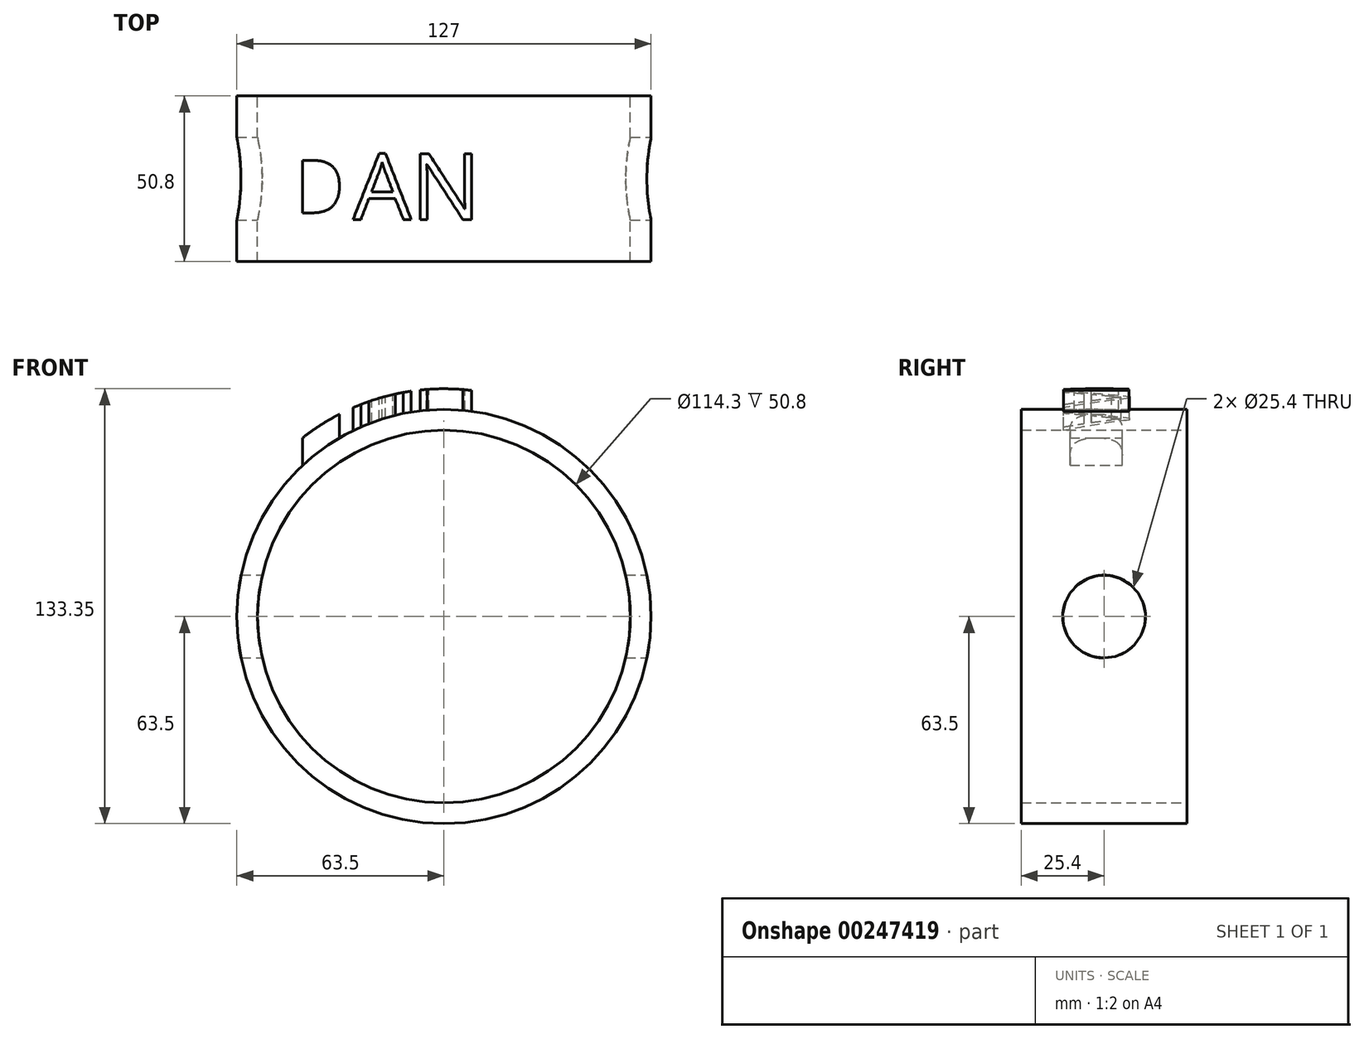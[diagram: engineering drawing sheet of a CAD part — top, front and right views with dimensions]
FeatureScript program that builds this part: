
annotation { "Feature Type Name" : "Feature", "Feature Type Description" : "" }
export const myFeature = defineFeature(function(context is Context, id is Id, definition is map)
    precondition{}
    {
        {
            var Q0;
            Q0=qCreatedBy(makeId("Front.planeOp"),FACE);
            var sketch = newSketch(context, id + "F0", { "sketchPlane" : qUnion([Q0])});
            skCircle(sketch, "E0", {"center": v(0, 0) * mm, "radius": 63.5 * mm});
            skCircle(sketch, "E1", {"center": v(0, 0) * mm, "radius": 57.15 * mm});
            skSolve(sketch);
        }
        {
            var Q0;
            Q0=makeQuery(id+"F0.imprint","IMPRINT",FACE,{"disambiguationData":[TD([[makeQuery(id+"F0.imprint","IMPRINT",EDGE,{"derivedFrom":sQuery(id+"F0.wireOp",EDGE,"E0")}),1.0]])]});
            extrude(context, id + "F1", {"entities" : qUnion([Q0]), "depth" : 50.8 * mm});
        }
        {
            var Q0;
            Q0=qCreatedBy(makeId("Top.planeOp"),FACE);
            cPlane(context, id + "F6", {"entities" : qUnion([Q0]), "cplaneType" : CPlaneType.OFFSET, "offset" : 76.2 * mm, "width" : 152.4 * mm, "height" : 152.4 * mm});
        }
        {
            var Q0;
            Q0=qCreatedBy(id+"F6.planeOp",FACE);
            var sketch = newSketch(context, id + "F2", { "sketchPlane" : qUnion([Q0])});
            skText(sketch, "E2", { "text": "DAN", "fontName": "OpenSans-Regular.ttf"});
            const initialGuessF2  = {"E2": [-0.0484, -0.03788, 1, 0, 0.02029]};
            skSetInitialGuess(sketch, initialGuessF2);
            skSolve(sketch);
        }
        {
            var Q0;
            Q0=makeQuery(id+"F2.imprint","IMPRINT",FACE,{"disambiguationData":[TD([[makeQuery(id+"F2.imprint","IMPRINT",EDGE,{"derivedFrom":sQuery(id+"F2.wireOp",EDGE,"E2.sketch_text.stroke-27")}),-1.0]])]});
            var Q1;
            Q1=makeQuery(id+"F2.imprint","IMPRINT",FACE,{"disambiguationData":[TD([[makeQuery(id+"F2.imprint","IMPRINT",EDGE,{"derivedFrom":sQuery(id+"F2.wireOp",EDGE,"E2.sketch_text.stroke-14")}),-1.0]])]});
            var Q2;
            Q2=makeQuery(id+"F2.imprint","IMPRINT",FACE,{"disambiguationData":[TD([[makeQuery(id+"F2.imprint","IMPRINT",EDGE,{"derivedFrom":sQuery(id+"F2.wireOp",EDGE,"E2.sketch_text.stroke-7")}),1.0]])]});
            extrude(context, id + "F3", {"entities" : qUnion([Q0, Q1, Q2]), "operationType" : NewBodyOperationType.ADD, "endBound" : BoundingType.UP_TO_NEXT, "oppositeDirection" : true, "depth" : 25.4 * mm});
        }
        {
            var Q0;
            Q0=qCreatedBy(makeId("Front.planeOp"),FACE);
            var sketch = newSketch(context, id + "F4", { "sketchPlane" : qUnion([Q0])});
            skCircle(sketch, "E3", {"center": v(0, 0) * mm, "radius": 69.85 * mm});
            skCircle(sketch, "E4", {"center": v(0, 0) * mm, "radius": 63.5 * mm});
            skCircle(sketch, "E5", {"center": v(3.91, 0.73) * mm, "radius": 117.58 * mm});
            skSolve(sketch);
        }
        {
            var Q0;
            Q0 = qSketchRegion(id + "F4", true);
            extrude(context, id + "F5", {"entities" : qUnion([Q0]), "operationType" : NewBodyOperationType.REMOVE, "endBound" : BoundingType.SYMMETRIC, "depth" : 152.4 * mm});
        }
        {
            var Q0;
            Q0=qCreatedBy(makeId("Right.planeOp"),FACE);
            var sketch = newSketch(context, id + "F7", { "sketchPlane" : qUnion([Q0])});
            skCircle(sketch, "E6", {"center": v(-25.4, 0) * mm, "radius": 12.7 * mm});
            skSolve(sketch);
        }
        {
            var Q0;
            Q0=makeQuery(id+"F7.imprint","IMPRINT",FACE,{"disambiguationData":[TD([[makeQuery(id+"F7.imprint","IMPRINT",EDGE,{"derivedFrom":sQuery(id+"F7.wireOp",EDGE,"E6")}),1.0]])]});
            extrude(context, id + "F8", {"entities" : qUnion([Q0]), "operationType" : NewBodyOperationType.REMOVE, "endBound" : BoundingType.SYMMETRIC, "oppositeDirection" : true, "depth" : 152.4 * mm});
        }
    });
